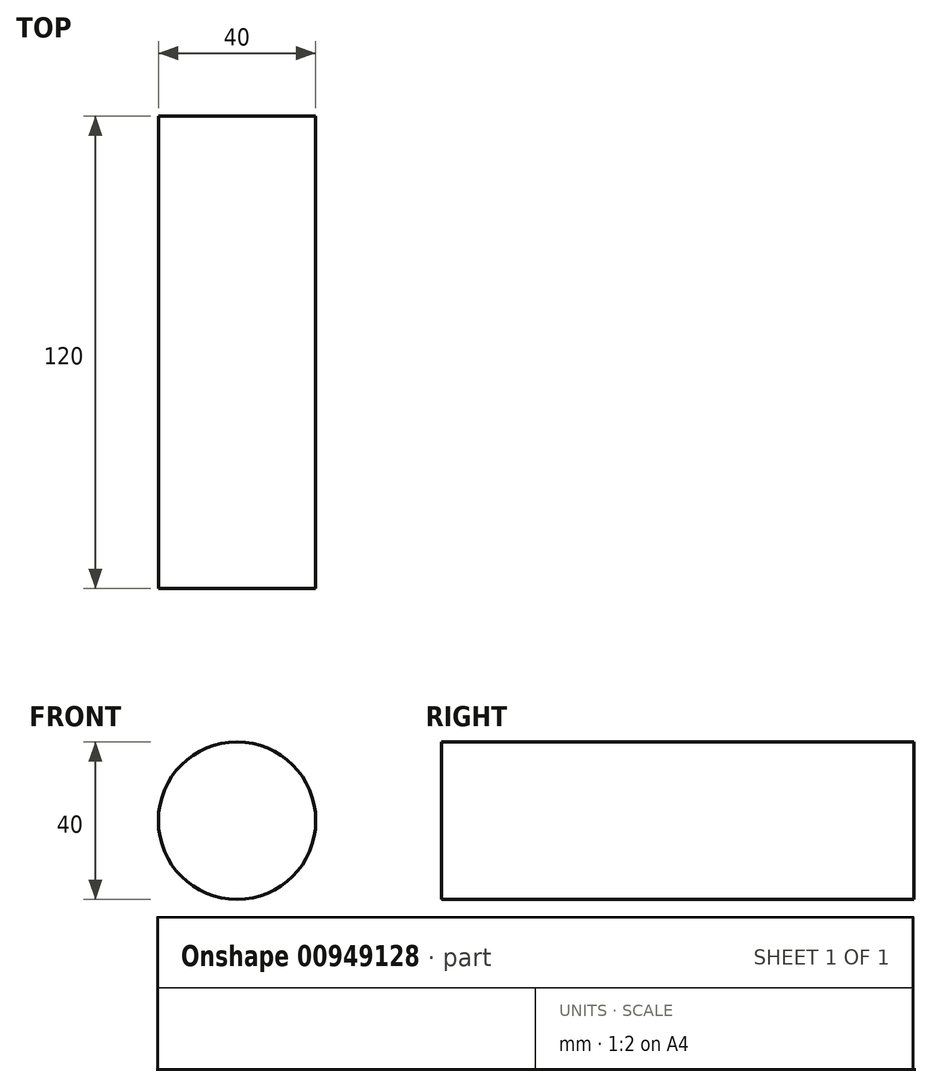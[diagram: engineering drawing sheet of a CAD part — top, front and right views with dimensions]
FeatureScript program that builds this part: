
annotation { "Feature Type Name" : "Feature", "Feature Type Description" : "" }
export const myFeature = defineFeature(function(context is Context, id is Id, definition is map)
    precondition{}
    {
        {
            var Q0;
            Q0=qCreatedBy(makeId("Front.planeOp"),FACE);
            var sketch = newSketch(context, id + "F0", { "sketchPlane" : qUnion([Q0])});
            skCircle(sketch, "E0", {"center": v(0, 0) * mm, "radius": 20 * mm});
            skSolve(sketch);
        }
        {
            var Q0;
            Q0=makeQuery(id+"F0.imprint","IMPRINT",FACE,{"disambiguationData":[TD([[makeQuery(id+"F0.imprint","IMPRINT",EDGE,{"derivedFrom":sQuery(id+"F0.wireOp",EDGE,"E0")}),1.0]])]});
            extrude(context, id + "F1", {"entities" : qUnion([Q0]), "endBound" : BoundingType.SYMMETRIC, "depth" : 120 * mm, "offsetDistance" : 25.4 * mm});
        }
    });
